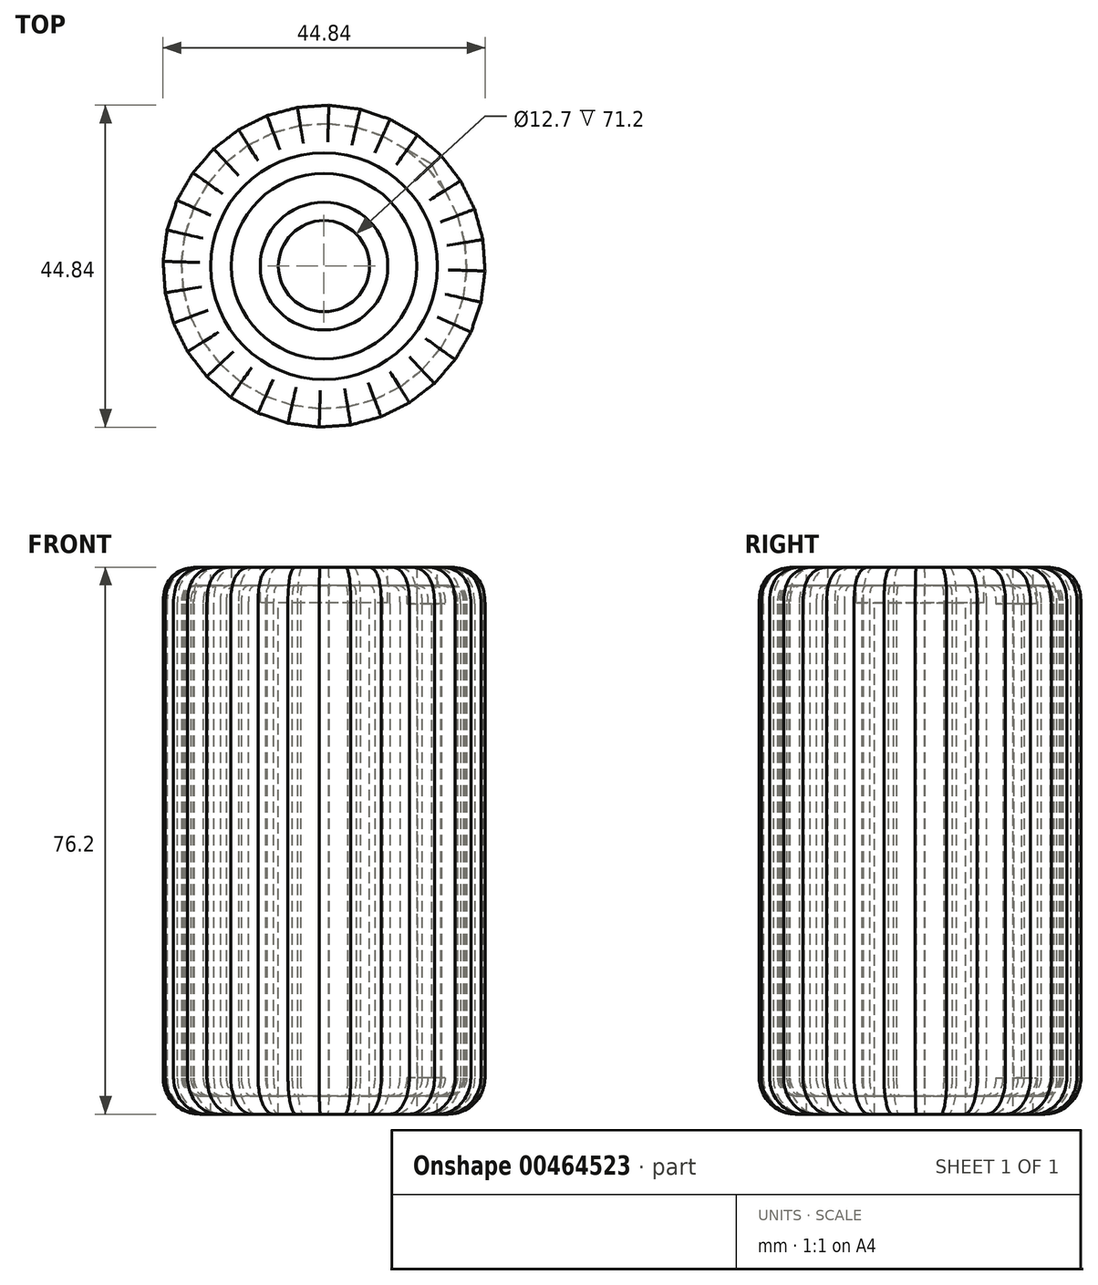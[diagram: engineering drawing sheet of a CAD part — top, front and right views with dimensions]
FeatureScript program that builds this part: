
annotation { "Feature Type Name" : "Feature", "Feature Type Description" : "" }
export const myFeature = defineFeature(function(context is Context, id is Id, definition is map)
    precondition{}
    {
        {
            var Q0;
            Q0=qCreatedBy(makeId("Top.planeOp"),FACE);
            var sketch = newSketch(context, id + "F0", { "sketchPlane" : qUnion([Q0])});
            skCircle(sketch, "E0.cCircle", {"center": v(0, 0) * mm, "radius": 22.32 * mm, "construction": true});
            skLineSegment(sketch, "E0.0", {"start": v(9.2, 20.46) * mm, "end": v(13.01, 18.27) * mm});
            skLineSegment(sketch, "E0.1", {"start": v(13.01, 18.27) * mm, "end": v(16.33, 15.38) * mm});
            skLineSegment(sketch, "E0.2", {"start": v(16.33, 15.38) * mm, "end": v(19.01, 11.9) * mm});
            skLineSegment(sketch, "E0.3", {"start": v(19.01, 11.9) * mm, "end": v(20.97, 7.96) * mm});
            skLineSegment(sketch, "E0.4", {"start": v(20.97, 7.96) * mm, "end": v(22.12, 3.72) * mm});
            skLineSegment(sketch, "E0.5", {"start": v(22.12, 3.72) * mm, "end": v(22.42, -0.67) * mm});
            skLineSegment(sketch, "E0.6", {"start": v(22.42, -0.67) * mm, "end": v(21.86, -5.03) * mm});
            skLineSegment(sketch, "E0.7", {"start": v(21.86, -5.03) * mm, "end": v(20.46, -9.2) * mm});
            skLineSegment(sketch, "E0.8", {"start": v(20.46, -9.2) * mm, "end": v(18.27, -13.01) * mm});
            skLineSegment(sketch, "E0.9", {"start": v(18.27, -13.01) * mm, "end": v(15.38, -16.33) * mm});
            skLineSegment(sketch, "E0.10", {"start": v(15.38, -16.33) * mm, "end": v(11.9, -19.01) * mm});
            skLineSegment(sketch, "E0.11", {"start": v(11.9, -19.01) * mm, "end": v(7.96, -20.97) * mm});
            skLineSegment(sketch, "E0.12", {"start": v(7.96, -20.97) * mm, "end": v(3.72, -22.12) * mm});
            skLineSegment(sketch, "E0.13", {"start": v(3.72, -22.12) * mm, "end": v(-0.67, -22.42) * mm});
            skLineSegment(sketch, "E0.14", {"start": v(-0.67, -22.42) * mm, "end": v(-5.03, -21.86) * mm});
            skLineSegment(sketch, "E0.15", {"start": v(-5.03, -21.86) * mm, "end": v(-9.2, -20.46) * mm});
            skLineSegment(sketch, "E0.16", {"start": v(-9.2, -20.46) * mm, "end": v(-13.01, -18.27) * mm});
            skLineSegment(sketch, "E0.17", {"start": v(-13.01, -18.27) * mm, "end": v(-16.33, -15.38) * mm});
            skLineSegment(sketch, "E0.18", {"start": v(-16.33, -15.38) * mm, "end": v(-19.01, -11.9) * mm});
            skLineSegment(sketch, "E0.19", {"start": v(-19.01, -11.9) * mm, "end": v(-20.97, -7.96) * mm});
            skLineSegment(sketch, "E0.20", {"start": v(-20.97, -7.96) * mm, "end": v(-22.12, -3.72) * mm});
            skLineSegment(sketch, "E0.21", {"start": v(-22.12, -3.72) * mm, "end": v(-22.42, 0.67) * mm});
            skLineSegment(sketch, "E0.22", {"start": v(-22.42, 0.67) * mm, "end": v(-21.86, 5.03) * mm});
            skLineSegment(sketch, "E0.23", {"start": v(-21.86, 5.03) * mm, "end": v(-20.46, 9.2) * mm});
            skLineSegment(sketch, "E0.24", {"start": v(-20.46, 9.2) * mm, "end": v(-18.27, 13.01) * mm});
            skLineSegment(sketch, "E0.25", {"start": v(-18.27, 13.01) * mm, "end": v(-15.38, 16.33) * mm});
            skLineSegment(sketch, "E0.26", {"start": v(-15.38, 16.33) * mm, "end": v(-11.9, 19.01) * mm});
            skLineSegment(sketch, "E0.27", {"start": v(-11.9, 19.01) * mm, "end": v(-7.96, 20.97) * mm});
            skLineSegment(sketch, "E0.28", {"start": v(-7.96, 20.97) * mm, "end": v(-3.72, 22.12) * mm});
            skLineSegment(sketch, "E0.29", {"start": v(-3.72, 22.12) * mm, "end": v(0.67, 22.42) * mm});
            skLineSegment(sketch, "E0.30", {"start": v(0.67, 22.42) * mm, "end": v(5.03, 21.86) * mm});
            skLineSegment(sketch, "E0.31", {"start": v(5.03, 21.86) * mm, "end": v(9.2, 20.46) * mm});
            skPoint(sketch, "E0.0.midPoint", {"position": v(11.1, 19.36) * mm});
            skSolve(sketch);
        }
        {
            var Q0;
            Q0=makeQuery(id+"F0.imprint","IMPRINT",FACE,{"disambiguationData":[TD([[makeQuery(id+"F0.imprint","IMPRINT",EDGE,{"derivedFrom":sQuery(id+"F0.wireOp",EDGE,"E0.0")}),-1.0]])]});
            extrude(context, id + "F1", {"entities" : qUnion([Q0]), "depth" : 76.2 * mm});
        }
        {
            var Q0;
            Q0=makeQuery(id+"F1.opExtrude","CAP_FACE",FACE,{"disambiguationData":[OSD([sQuery(id+"F0.wireOp",EDGE,"E0.0"),sQuery(id+"F0.wireOp",EDGE,"E0.1"),sQuery(id+"F0.wireOp",EDGE,"E0.2"),sQuery(id+"F0.wireOp",EDGE,"E0.3"),sQuery(id+"F0.wireOp",EDGE,"E0.4"),sQuery(id+"F0.wireOp",EDGE,"E0.5"),sQuery(id+"F0.wireOp",EDGE,"E0.6"),sQuery(id+"F0.wireOp",EDGE,"E0.7"),sQuery(id+"F0.wireOp",EDGE,"E0.8"),sQuery(id+"F0.wireOp",EDGE,"E0.9"),sQuery(id+"F0.wireOp",EDGE,"E0.10"),sQuery(id+"F0.wireOp",EDGE,"E0.11"),sQuery(id+"F0.wireOp",EDGE,"E0.12"),sQuery(id+"F0.wireOp",EDGE,"E0.13"),sQuery(id+"F0.wireOp",EDGE,"E0.14"),sQuery(id+"F0.wireOp",EDGE,"E0.15"),sQuery(id+"F0.wireOp",EDGE,"E0.16"),sQuery(id+"F0.wireOp",EDGE,"E0.17"),sQuery(id+"F0.wireOp",EDGE,"E0.18"),sQuery(id+"F0.wireOp",EDGE,"E0.19"),sQuery(id+"F0.wireOp",EDGE,"E0.20"),sQuery(id+"F0.wireOp",EDGE,"E0.21"),sQuery(id+"F0.wireOp",EDGE,"E0.22"),sQuery(id+"F0.wireOp",EDGE,"E0.23"),sQuery(id+"F0.wireOp",EDGE,"E0.24"),sQuery(id+"F0.wireOp",EDGE,"E0.25"),sQuery(id+"F0.wireOp",EDGE,"E0.26"),sQuery(id+"F0.wireOp",EDGE,"E0.27"),sQuery(id+"F0.wireOp",EDGE,"E0.28"),sQuery(id+"F0.wireOp",EDGE,"E0.29"),sQuery(id+"F0.wireOp",EDGE,"E0.30"),sQuery(id+"F0.wireOp",EDGE,"E0.31")])],"isStart":false});
            fillet(context, id + "F2", {"entities" : qUnion([Q0]), "radius" : 5.08 * mm, "tangentPropagation" : true, "rho" : 0.5, "crossSection" : FilletCrossSection.CONIC, "allowEdgeOverflow" : false});
        }
        {
            var Q0;
            Q0=makeQuery(id+"F1.opExtrude","CAP_FACE",FACE,{"disambiguationData":[OSD([sQuery(id+"F0.wireOp",EDGE,"E0.0"),sQuery(id+"F0.wireOp",EDGE,"E0.1"),sQuery(id+"F0.wireOp",EDGE,"E0.2"),sQuery(id+"F0.wireOp",EDGE,"E0.3"),sQuery(id+"F0.wireOp",EDGE,"E0.4"),sQuery(id+"F0.wireOp",EDGE,"E0.5"),sQuery(id+"F0.wireOp",EDGE,"E0.6"),sQuery(id+"F0.wireOp",EDGE,"E0.7"),sQuery(id+"F0.wireOp",EDGE,"E0.8"),sQuery(id+"F0.wireOp",EDGE,"E0.9"),sQuery(id+"F0.wireOp",EDGE,"E0.10"),sQuery(id+"F0.wireOp",EDGE,"E0.11"),sQuery(id+"F0.wireOp",EDGE,"E0.12"),sQuery(id+"F0.wireOp",EDGE,"E0.13"),sQuery(id+"F0.wireOp",EDGE,"E0.14"),sQuery(id+"F0.wireOp",EDGE,"E0.15"),sQuery(id+"F0.wireOp",EDGE,"E0.16"),sQuery(id+"F0.wireOp",EDGE,"E0.17"),sQuery(id+"F0.wireOp",EDGE,"E0.18"),sQuery(id+"F0.wireOp",EDGE,"E0.19"),sQuery(id+"F0.wireOp",EDGE,"E0.20"),sQuery(id+"F0.wireOp",EDGE,"E0.21"),sQuery(id+"F0.wireOp",EDGE,"E0.22"),sQuery(id+"F0.wireOp",EDGE,"E0.23"),sQuery(id+"F0.wireOp",EDGE,"E0.24"),sQuery(id+"F0.wireOp",EDGE,"E0.25"),sQuery(id+"F0.wireOp",EDGE,"E0.26"),sQuery(id+"F0.wireOp",EDGE,"E0.27"),sQuery(id+"F0.wireOp",EDGE,"E0.28"),sQuery(id+"F0.wireOp",EDGE,"E0.29"),sQuery(id+"F0.wireOp",EDGE,"E0.30"),sQuery(id+"F0.wireOp",EDGE,"E0.31")])],"isStart":true});
            fillet(context, id + "F3", {"entities" : qUnion([Q0]), "radius" : 5.08 * mm, "tangentPropagation" : true, "allowEdgeOverflow" : false});
        }
        {
            var Q0;
            Q0=qCreatedBy(makeId("Top.planeOp"),FACE);
            var sketch = newSketch(context, id + "F4", { "sketchPlane" : qUnion([Q0])});
            skPoint(sketch, "E1", {"position": v(-52.64, 21.05) * mm});
            skPoint(sketch, "E2", {"position": v(0, 0) * mm});
            skCircle(sketch, "E3", {"center": v(0, 0) * mm, "radius": 6.57 * mm});
            skSolve(sketch);
        }
        {
            var Q0;
            Q0=sQuery(id+"F4.wireOp",VERTEX,"E2");
            var Q1;
            Q1=makeQuery(id+"F1.opExtrude","SWEPT_BODY",BODY,{"disambiguationData":[OSD([sQuery(id+"F0.wireOp",EDGE,"E0.0"),sQuery(id+"F0.wireOp",EDGE,"E0.1"),sQuery(id+"F0.wireOp",EDGE,"E0.2"),sQuery(id+"F0.wireOp",EDGE,"E0.3"),sQuery(id+"F0.wireOp",EDGE,"E0.4"),sQuery(id+"F0.wireOp",EDGE,"E0.5"),sQuery(id+"F0.wireOp",EDGE,"E0.6"),sQuery(id+"F0.wireOp",EDGE,"E0.7"),sQuery(id+"F0.wireOp",EDGE,"E0.8"),sQuery(id+"F0.wireOp",EDGE,"E0.9"),sQuery(id+"F0.wireOp",EDGE,"E0.10"),sQuery(id+"F0.wireOp",EDGE,"E0.11"),sQuery(id+"F0.wireOp",EDGE,"E0.12"),sQuery(id+"F0.wireOp",EDGE,"E0.13"),sQuery(id+"F0.wireOp",EDGE,"E0.14"),sQuery(id+"F0.wireOp",EDGE,"E0.15"),sQuery(id+"F0.wireOp",EDGE,"E0.16"),sQuery(id+"F0.wireOp",EDGE,"E0.17"),sQuery(id+"F0.wireOp",EDGE,"E0.18"),sQuery(id+"F0.wireOp",EDGE,"E0.19"),sQuery(id+"F0.wireOp",EDGE,"E0.20"),sQuery(id+"F0.wireOp",EDGE,"E0.21"),sQuery(id+"F0.wireOp",EDGE,"E0.22"),sQuery(id+"F0.wireOp",EDGE,"E0.23"),sQuery(id+"F0.wireOp",EDGE,"E0.24"),sQuery(id+"F0.wireOp",EDGE,"E0.25"),sQuery(id+"F0.wireOp",EDGE,"E0.26"),sQuery(id+"F0.wireOp",EDGE,"E0.27"),sQuery(id+"F0.wireOp",EDGE,"E0.28"),sQuery(id+"F0.wireOp",EDGE,"E0.29"),sQuery(id+"F0.wireOp",EDGE,"E0.30"),sQuery(id+"F0.wireOp",EDGE,"E0.31")])]});
            hole(context, id + "F5", {"style" : HoleStyle.C_SINK, "endStyle" : HoleEndStyle.BLIND, "oppositeDirection" : true, "standardTappedOrClearance" : lookupTablePath({ "standard" : "ISO", "size" : "4.2", "type" : "Drilled" }), "standardBlindInLast" : lookupTablePath({ "standard" : "ISO", "size" : "4.2", "type" : "Drilled" }), "holeDiameter" : 4.2 * mm, "cSinkDiameter" : 11.2 * mm, "cSinkAngle" : 90 * degree, "holeDepth" : 12.7 * mm, "isTappedThrough" : true, "tappedDepth" : 12.7 * mm, "tapClearance" : 3, "locations" : qUnion([Q0]), "scope" : qUnion([Q1])});
        }
        {
            var Q0;
            Q0=makeQuery(id+"F1.opExtrude","SWEPT_FACE",FACE,{"disambiguationData":[OSD([sQuery(id+"F0.wireOp",EDGE,"E0.1")])]});
            var Q1;
            Q1=makeQuery(id+"F1.opExtrude","SWEPT_FACE",FACE,{"disambiguationData":[OSD([sQuery(id+"F0.wireOp",EDGE,"E0.2")])]});
            shell(context, id + "F6", {"entities" : qUnion([Q0, Q1]), "thickness" : 2.54 * mm});
        }
        {
            var Q0;
            Q0=qCreatedBy(makeId("Top.planeOp"),FACE);
            cPlane(context, id + "F7", {"entities" : qUnion([Q0]), "cplaneType" : CPlaneType.OFFSET, "offset" : 76.2 * mm, "width" : 152.4 * mm, "height" : 152.4 * mm});
        }
        {
            var Q0;
            Q0=qCreatedBy(id+"F7.planeOp",FACE);
            var sketch = newSketch(context, id + "F8", { "sketchPlane" : qUnion([Q0])});
            skCircle(sketch, "E4", {"center": v(0, 0) * mm, "radius": 15.78 * mm});
            skSolve(sketch);
        }
        {
            var Q0;
            Q0=makeQuery(id+"F8.imprint","IMPRINT",FACE,{"disambiguationData":[TD([[makeQuery(id+"F8.imprint","IMPRINT",EDGE,{"derivedFrom":sQuery(id+"F8.wireOp",EDGE,"E4")}),1.0]])]});
            extrude(context, id + "F9", {"entities" : qUnion([Q0]), "operationType" : NewBodyOperationType.REMOVE, "endBound" : BoundingType.THROUGH_ALL, "oppositeDirection" : true, "depth" : 25.4 * mm});
        }
        {
            var Q0;
            Q0=qCreatedBy(makeId("Top.planeOp"),FACE);
            var sketch = newSketch(context, id + "F10", { "sketchPlane" : qUnion([Q0])});
            skCircle(sketch, "E5", {"center": v(0, 0) * mm, "radius": 12.91 * mm});
            skSolve(sketch);
        }
        {
            var Q0;
            Q0 = qSketchRegion(id + "F10", true);
            extrude(context, id + "F11", {"entities" : qUnion([Q0]), "depth" : 76.2 * mm});
        }
        {
            var Q0;
            Q0=qCreatedBy(id+"F7.planeOp",FACE);
            var sketch = newSketch(context, id + "F12", { "sketchPlane" : qUnion([Q0])});
            skPoint(sketch, "E6", {"position": v(0, 0) * mm});
            skSolve(sketch);
        }
        {
            var Q0;
            Q0=sQuery(id+"F12.wireOp",VERTEX,"E6");
            var Q1;
            Q1=makeQuery(id+"F11.opExtrude","SWEPT_BODY",BODY,{"disambiguationData":[OSD([sQuery(id+"F10.wireOp",EDGE,"E5")])]});
            hole(context, id + "F13", {"style" : HoleStyle.C_BORE, "endStyle" : HoleEndStyle.BLIND, "holeDiameter" : 12.7 * mm, "cBoreDiameter" : 17.78 * mm, "cBoreDepth" : 5 * mm, "holeDepth" : 127 * mm, "isTappedThrough" : true, "tappedDepth" : 12.7 * mm, "tapClearance" : 3, "locations" : qUnion([Q0]), "scope" : qUnion([Q1])});
        }
    });
